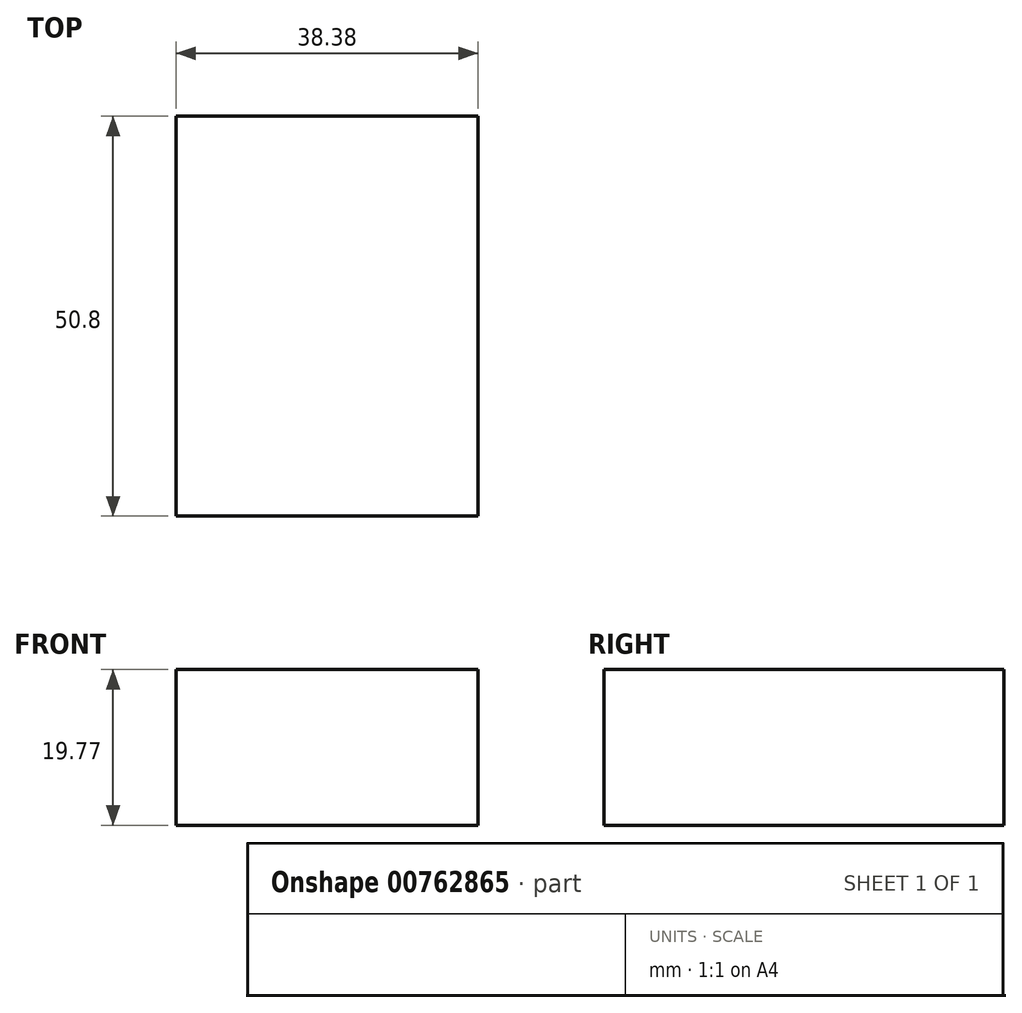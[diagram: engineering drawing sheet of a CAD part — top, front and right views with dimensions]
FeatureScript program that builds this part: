
annotation { "Feature Type Name" : "Feature", "Feature Type Description" : "" }
export const myFeature = defineFeature(function(context is Context, id is Id, definition is map)
    precondition{}
    {
        {
            var Q0;
            Q0=qCreatedBy(makeId("Front.planeOp"),FACE);
            var sketch = newSketch(context, id + "F0", { "sketchPlane" : qUnion([Q0])});
            skLineSegment(sketch, "E0.bottom", {"start": v(0, 0) * mm, "end": v(38.38, 0) * mm});
            skLineSegment(sketch, "E0.top", {"start": v(0, 19.77) * mm, "end": v(38.38, 19.77) * mm});
            skLineSegment(sketch, "E0.left", {"start": v(0, 0) * mm, "end": v(0, 19.77) * mm});
            skLineSegment(sketch, "E0.right", {"start": v(38.38, 0) * mm, "end": v(38.38, 19.77) * mm});
            skSolve(sketch);
        }
        {
            var Q0;
            Q0=makeQuery(id+"F0.imprint","IMPRINT",FACE,{"disambiguationData":[TD([[makeQuery(id+"F0.imprint","IMPRINT",EDGE,{"derivedFrom":sQuery(id+"F0.wireOp",EDGE,"E0.bottom")}),1.0]])]});
            extrude(context, id + "F1", {"entities" : qUnion([Q0]), "depth" : 50.8 * mm, "offsetDistance" : 25.4 * mm});
        }
    });
